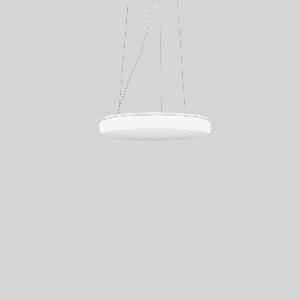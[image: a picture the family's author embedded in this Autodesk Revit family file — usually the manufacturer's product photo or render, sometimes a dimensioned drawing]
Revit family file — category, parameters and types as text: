
# Revit family: flat_polymero_kreis_slim_312090_002_3_76_2ffd
name_source: partatom
category: Lighting Fixtures
units: mm (PartAtom-declared; Revit-internal decimal feet)

## family parameters
Cut with Voids When Loaded = No
Host = Face
Light Source = No
Part Type = Normal
Room Calculation Point = No
Round Connector Dimension = Use Diameter
Shared = No

## types (1)
- FLAT POLYMERO KREIS SLIM (1 x LED Modul 840, 2100 lm, 4000)
    Apparent Load = 19 VA
    CIE Flux Codes = 43 74 93 88 100
    Color Rendering = 80
    Color Temperature = 4000
    Default Elevation = 1800 mm
    Description = Series: FLAT POLYMERO KREIS SLIM
Decorative round LED pendant luminaire. Base and canopy: metal, powder-coated, white. Canopy Ø 205 mm, h 35 mm. Diffuser made of non-yellowing plastic (PMMA), opal. Diffuser fastening: patented push system. Homogeneous and smooth light distribution. Suitable for pendant. 3-point steel cable suspension, steplessly adjustable. Special lengths available on request. TouchDim sensor capable. Light and/or presence sensors can be integrated. 
Colour: white
Diameter: 460 mm
Height: 68 mm
Suspension length: 200-1300 mm
Lamp: LED
Socket: without socket
Colour temperature: 4000K
Colour rendering index (CRI): 80
System power: 19 W
Rated luminous flux: 2100 lm
Luminous efficiency: 111 lm/W
Control gear: AC power, DALI dimmable
Protection class: I
Type of protection: IP 40
    Height = 68 mm
    Lamp = 1 x LED Modul 840
    Lamp Light Flux = 2100 lm
    Lamp count = 1
    Length = 460 mm
    Lifetime = 50000 h
    Luminous efficacy = 111 lm/W
    Manufacturer = RZB
    ModVariant = No
    Model = 312090.002.3.76
    Mounting Place = Ceiling
    Mounting Type = Pendant
    Number of Poles = 1
    OnlyDefault = Yes
    Power Factor = 1
    Product Name = FLAT POLYMERO KREIS SLIM
    Product group = Pendant luminaires
    ProductGroupID = 902
    Protection Class = Protection class I
    Protection Degree = IP 40
    RLX_Detail_Level = 1
    RLX_Emergency_Light_Flux = 0 lm
    RLX_Emergency_Type = 0
    RLX_Emergency_Type_DB = No
    RlxData = <blob elided: 58497 chars, md5=63847f01>
    Socket = socket
    Standby Power = 0 W
    System Light Flux = 2100 lm
    System Power = 19 W
    Type Comments = Product without accessories
    Type Image = 312090.002.jpg
    URL = http://relux.com
    VarID = ---
    Voltage = 230 V
    Voltage Range = 220-240 V
    Weight = 0.00 kg
    Width = 0 mm  [stored 0 ft]

note: [stored X ft] marks values corroborated as IEEE doubles in the binary element streams (Revit-internal decimal feet)

## geometry (parser evidence)
native form markers: Blend x4, Sweep x13
no freeform markers — native parametric forms only
